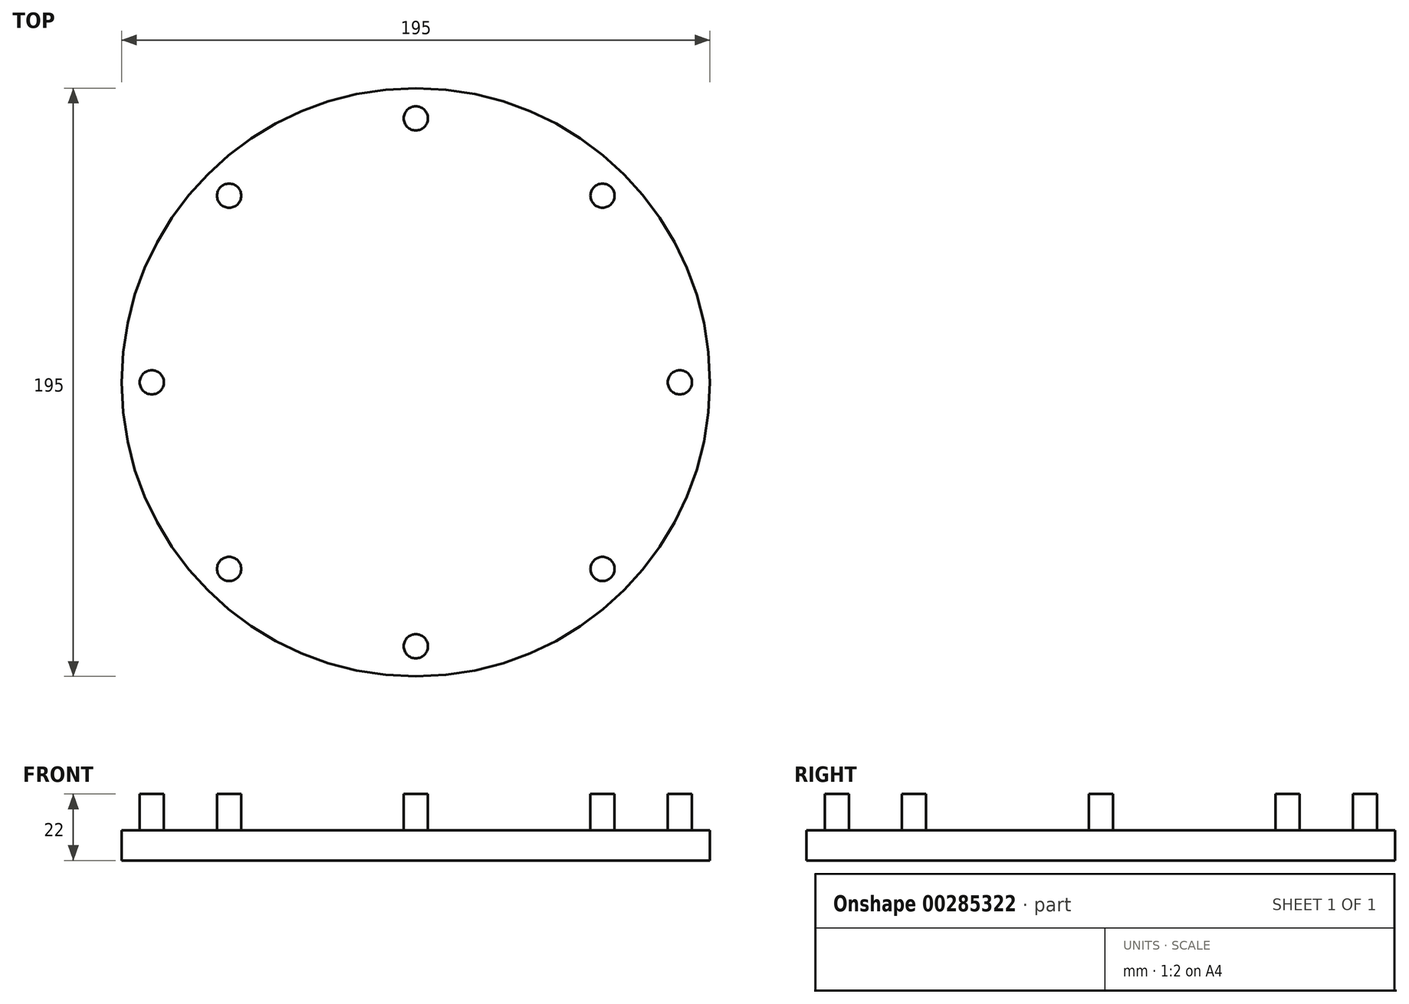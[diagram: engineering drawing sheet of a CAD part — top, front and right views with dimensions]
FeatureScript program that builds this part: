
annotation { "Feature Type Name" : "Feature", "Feature Type Description" : "" }
export const myFeature = defineFeature(function(context is Context, id is Id, definition is map)
    precondition{}
    {
        {
            var Q0;
            Q0=qCreatedBy(makeId("Top.planeOp"),FACE);
            var sketch = newSketch(context, id + "F0", { "sketchPlane" : qUnion([Q0])});
            skCircle(sketch, "E0", {"center": v(0, 0) * mm, "radius": 97.5 * mm});
            skCircle(sketch, "E1.cCircle", {"center": v(0, 0) * mm, "radius": 87.5 * mm, "construction": true});
            skLineSegment(sketch, "E1.0", {"start": v(87.5, 0) * mm, "end": v(61.87, -61.87) * mm});
            skLineSegment(sketch, "E1.1", {"start": v(61.87, -61.87) * mm, "end": v(0, -87.5) * mm});
            skLineSegment(sketch, "E1.2", {"start": v(0, -87.5) * mm, "end": v(-61.87, -61.87) * mm});
            skLineSegment(sketch, "E1.3", {"start": v(-61.87, -61.87) * mm, "end": v(-87.5, 0) * mm});
            skLineSegment(sketch, "E1.4", {"start": v(-87.5, 0) * mm, "end": v(-61.87, 61.87) * mm});
            skLineSegment(sketch, "E1.5", {"start": v(-61.87, 61.87) * mm, "end": v(0, 87.5) * mm});
            skLineSegment(sketch, "E1.6", {"start": v(0, 87.5) * mm, "end": v(61.87, 61.87) * mm});
            skLineSegment(sketch, "E1.7", {"start": v(61.87, 61.87) * mm, "end": v(87.5, 0) * mm});
            skCircle(sketch, "E2", {"center": v(0, 87.5) * mm, "radius": 4 * mm});
            skCircle(sketch, "E3", {"center": v(61.87, 61.87) * mm, "radius": 4 * mm});
            skCircle(sketch, "E4", {"center": v(87.5, 0) * mm, "radius": 4 * mm});
            skCircle(sketch, "E5", {"center": v(61.87, -61.87) * mm, "radius": 4 * mm});
            skCircle(sketch, "E6", {"center": v(0, -87.5) * mm, "radius": 4 * mm});
            skCircle(sketch, "E7", {"center": v(-61.87, -61.87) * mm, "radius": 4 * mm});
            skCircle(sketch, "E8", {"center": v(-87.5, 0) * mm, "radius": 4 * mm});
            skCircle(sketch, "E9", {"center": v(-61.87, 61.87) * mm, "radius": 4 * mm});
            skSolve(sketch);
        }
        {
            var Q0;
            {var subQ3=sQuery(id+"F0.wireOp",EDGE,"E4");var subQ15=sQuery(id+"F0.wireOp",EDGE,"E1.0");var subQ16=makeQuery(id+"F0.imprint","INTERSECT",VERTEX,{"derivedFrom":[subQ15,subQ3]});Q0=makeQuery(id+"F0.imprint","IMPRINT",FACE,{"disambiguationData":[TD([[makeQuery(id+"F0.imprint","IMPRINT",EDGE,{"disambiguationData":[TD([[subQ16,-1.0]])],"derivedFrom":subQ15}),-1.0]])]});}
            var Q1;
            {var subQ0=sQuery(id+"F0.wireOp",EDGE,"E1.5");var subQ1=sQuery(id+"F0.wireOp",EDGE,"E1.4");var subQ2=makeQuery(id+"F0.imprint","INTERSECT",VERTEX,{"derivedFrom":[subQ1,subQ0]});Q1=makeQuery(id+"F0.imprint","IMPRINT",FACE,{"disambiguationData":[TD([[makeQuery(id+"F0.imprint","IMPRINT",EDGE,{"disambiguationData":[TD([[subQ2,1.0]])],"derivedFrom":subQ1}),1.0]])]});}
            var Q2;
            {var subQ0=sQuery(id+"F0.wireOp",EDGE,"E1.5");var subQ1=sQuery(id+"F0.wireOp",EDGE,"E1.4");var subQ2=makeQuery(id+"F0.imprint","INTERSECT",VERTEX,{"derivedFrom":[subQ1,subQ0]});Q2=makeQuery(id+"F0.imprint","IMPRINT",FACE,{"disambiguationData":[TD([[makeQuery(id+"F0.imprint","IMPRINT",EDGE,{"disambiguationData":[TD([[subQ2,1.0]])],"derivedFrom":subQ1}),-1.0]])]});}
            var Q3;
            Q3=makeQuery(id+"F0.imprint","IMPRINT",FACE,{"disambiguationData":[TD([[makeQuery(id+"F0.imprint","IMPRINT",EDGE,{"derivedFrom":sQuery(id+"F0.wireOp",EDGE,"E0")}),1.0]])]});
            var Q4;
            {var subQ0=sQuery(id+"F0.wireOp",EDGE,"E1.6");var subQ1=sQuery(id+"F0.wireOp",EDGE,"E1.5");var subQ2=makeQuery(id+"F0.imprint","INTERSECT",VERTEX,{"derivedFrom":[subQ1,subQ0]});Q4=makeQuery(id+"F0.imprint","IMPRINT",FACE,{"disambiguationData":[TD([[makeQuery(id+"F0.imprint","IMPRINT",EDGE,{"disambiguationData":[TD([[subQ2,1.0]])],"derivedFrom":subQ1}),1.0]])]});}
            var Q5;
            {var subQ0=sQuery(id+"F0.wireOp",EDGE,"E1.6");var subQ1=sQuery(id+"F0.wireOp",EDGE,"E1.5");var subQ2=makeQuery(id+"F0.imprint","INTERSECT",VERTEX,{"derivedFrom":[subQ1,subQ0]});Q5=makeQuery(id+"F0.imprint","IMPRINT",FACE,{"disambiguationData":[TD([[makeQuery(id+"F0.imprint","IMPRINT",EDGE,{"disambiguationData":[TD([[subQ2,1.0]])],"derivedFrom":subQ1}),-1.0]])]});}
            var Q6;
            {var subQ0=sQuery(id+"F0.wireOp",EDGE,"E1.7");var subQ1=sQuery(id+"F0.wireOp",EDGE,"E1.6");var subQ2=makeQuery(id+"F0.imprint","INTERSECT",VERTEX,{"derivedFrom":[subQ1,subQ0]});Q6=makeQuery(id+"F0.imprint","IMPRINT",FACE,{"disambiguationData":[TD([[makeQuery(id+"F0.imprint","IMPRINT",EDGE,{"disambiguationData":[TD([[subQ2,1.0]])],"derivedFrom":subQ1}),-1.0]])]});}
            var Q7;
            {var subQ0=sQuery(id+"F0.wireOp",EDGE,"E1.7");var subQ1=sQuery(id+"F0.wireOp",EDGE,"E1.6");var subQ2=makeQuery(id+"F0.imprint","INTERSECT",VERTEX,{"derivedFrom":[subQ1,subQ0]});Q7=makeQuery(id+"F0.imprint","IMPRINT",FACE,{"disambiguationData":[TD([[makeQuery(id+"F0.imprint","IMPRINT",EDGE,{"disambiguationData":[TD([[subQ2,1.0]])],"derivedFrom":subQ1}),1.0]])]});}
            var Q8;
            {var subQ0=sQuery(id+"F0.wireOp",EDGE,"E1.7");var subQ1=sQuery(id+"F0.wireOp",EDGE,"E1.0");var subQ2=makeQuery(id+"F0.imprint","INTERSECT",VERTEX,{"derivedFrom":[subQ1,subQ0]});Q8=makeQuery(id+"F0.imprint","IMPRINT",FACE,{"disambiguationData":[TD([[makeQuery(id+"F0.imprint","IMPRINT",EDGE,{"disambiguationData":[TD([[subQ2,-1.0]])],"derivedFrom":subQ1}),-1.0]])]});}
            var Q9;
            {var subQ0=sQuery(id+"F0.wireOp",EDGE,"E1.7");var subQ1=sQuery(id+"F0.wireOp",EDGE,"E1.0");var subQ2=makeQuery(id+"F0.imprint","INTERSECT",VERTEX,{"derivedFrom":[subQ1,subQ0]});Q9=makeQuery(id+"F0.imprint","IMPRINT",FACE,{"disambiguationData":[TD([[makeQuery(id+"F0.imprint","IMPRINT",EDGE,{"disambiguationData":[TD([[subQ2,-1.0]])],"derivedFrom":subQ1}),1.0]])]});}
            var Q10;
            {var subQ0=sQuery(id+"F0.wireOp",EDGE,"E1.1");var subQ1=sQuery(id+"F0.wireOp",EDGE,"E1.0");var subQ2=makeQuery(id+"F0.imprint","INTERSECT",VERTEX,{"derivedFrom":[subQ1,subQ0]});Q10=makeQuery(id+"F0.imprint","IMPRINT",FACE,{"disambiguationData":[TD([[makeQuery(id+"F0.imprint","IMPRINT",EDGE,{"disambiguationData":[TD([[subQ2,1.0]])],"derivedFrom":subQ1}),-1.0]])]});}
            var Q11;
            {var subQ0=sQuery(id+"F0.wireOp",EDGE,"E1.1");var subQ1=sQuery(id+"F0.wireOp",EDGE,"E1.0");var subQ2=makeQuery(id+"F0.imprint","INTERSECT",VERTEX,{"derivedFrom":[subQ1,subQ0]});Q11=makeQuery(id+"F0.imprint","IMPRINT",FACE,{"disambiguationData":[TD([[makeQuery(id+"F0.imprint","IMPRINT",EDGE,{"disambiguationData":[TD([[subQ2,1.0]])],"derivedFrom":subQ1}),1.0]])]});}
            var Q12;
            {var subQ0=sQuery(id+"F0.wireOp",EDGE,"E1.2");var subQ1=sQuery(id+"F0.wireOp",EDGE,"E1.1");var subQ2=makeQuery(id+"F0.imprint","INTERSECT",VERTEX,{"derivedFrom":[subQ1,subQ0]});Q12=makeQuery(id+"F0.imprint","IMPRINT",FACE,{"disambiguationData":[TD([[makeQuery(id+"F0.imprint","IMPRINT",EDGE,{"disambiguationData":[TD([[subQ2,1.0]])],"derivedFrom":subQ1}),-1.0]])]});}
            var Q13;
            {var subQ0=sQuery(id+"F0.wireOp",EDGE,"E1.2");var subQ1=sQuery(id+"F0.wireOp",EDGE,"E1.1");var subQ2=makeQuery(id+"F0.imprint","INTERSECT",VERTEX,{"derivedFrom":[subQ1,subQ0]});Q13=makeQuery(id+"F0.imprint","IMPRINT",FACE,{"disambiguationData":[TD([[makeQuery(id+"F0.imprint","IMPRINT",EDGE,{"disambiguationData":[TD([[subQ2,1.0]])],"derivedFrom":subQ1}),1.0]])]});}
            var Q14;
            {var subQ0=sQuery(id+"F0.wireOp",EDGE,"E1.3");var subQ1=sQuery(id+"F0.wireOp",EDGE,"E1.2");var subQ2=makeQuery(id+"F0.imprint","INTERSECT",VERTEX,{"derivedFrom":[subQ1,subQ0]});Q14=makeQuery(id+"F0.imprint","IMPRINT",FACE,{"disambiguationData":[TD([[makeQuery(id+"F0.imprint","IMPRINT",EDGE,{"disambiguationData":[TD([[subQ2,1.0]])],"derivedFrom":subQ1}),-1.0]])]});}
            var Q15;
            {var subQ0=sQuery(id+"F0.wireOp",EDGE,"E1.3");var subQ1=sQuery(id+"F0.wireOp",EDGE,"E1.2");var subQ2=makeQuery(id+"F0.imprint","INTERSECT",VERTEX,{"derivedFrom":[subQ1,subQ0]});Q15=makeQuery(id+"F0.imprint","IMPRINT",FACE,{"disambiguationData":[TD([[makeQuery(id+"F0.imprint","IMPRINT",EDGE,{"disambiguationData":[TD([[subQ2,1.0]])],"derivedFrom":subQ1}),1.0]])]});}
            var Q16;
            {var subQ0=sQuery(id+"F0.wireOp",EDGE,"E1.4");var subQ1=sQuery(id+"F0.wireOp",EDGE,"E1.3");var subQ2=makeQuery(id+"F0.imprint","INTERSECT",VERTEX,{"derivedFrom":[subQ1,subQ0]});Q16=makeQuery(id+"F0.imprint","IMPRINT",FACE,{"disambiguationData":[TD([[makeQuery(id+"F0.imprint","IMPRINT",EDGE,{"disambiguationData":[TD([[subQ2,1.0]])],"derivedFrom":subQ1}),-1.0]])]});}
            var Q17;
            {var subQ0=sQuery(id+"F0.wireOp",EDGE,"E1.4");var subQ1=sQuery(id+"F0.wireOp",EDGE,"E1.3");var subQ2=makeQuery(id+"F0.imprint","INTERSECT",VERTEX,{"derivedFrom":[subQ1,subQ0]});Q17=makeQuery(id+"F0.imprint","IMPRINT",FACE,{"disambiguationData":[TD([[makeQuery(id+"F0.imprint","IMPRINT",EDGE,{"disambiguationData":[TD([[subQ2,1.0]])],"derivedFrom":subQ1}),1.0]])]});}
            extrude(context, id + "F1", {"entities" : qUnion([Q0, Q1, Q2, Q3, Q4, Q5, Q6, Q7, Q8, Q9, Q10, Q11, Q12, Q13, Q14, Q15, Q16, Q17]), "depth" : 10 * mm});
        }
        {
            var Q0;
            {var subQ0=sQuery(id+"F0.wireOp",EDGE,"E1.6");var subQ1=sQuery(id+"F0.wireOp",EDGE,"E1.5");var subQ2=makeQuery(id+"F0.imprint","INTERSECT",VERTEX,{"derivedFrom":[subQ1,subQ0]});Q0=makeQuery(id+"F0.imprint","IMPRINT",FACE,{"disambiguationData":[TD([[makeQuery(id+"F0.imprint","IMPRINT",EDGE,{"disambiguationData":[TD([[subQ2,1.0]])],"derivedFrom":subQ1}),1.0]])]});}
            var Q1;
            {var subQ0=sQuery(id+"F0.wireOp",EDGE,"E1.6");var subQ1=sQuery(id+"F0.wireOp",EDGE,"E1.5");var subQ2=makeQuery(id+"F0.imprint","INTERSECT",VERTEX,{"derivedFrom":[subQ1,subQ0]});Q1=makeQuery(id+"F0.imprint","IMPRINT",FACE,{"disambiguationData":[TD([[makeQuery(id+"F0.imprint","IMPRINT",EDGE,{"disambiguationData":[TD([[subQ2,1.0]])],"derivedFrom":subQ1}),-1.0]])]});}
            var Q2;
            {var subQ0=sQuery(id+"F0.wireOp",EDGE,"E1.5");var subQ1=sQuery(id+"F0.wireOp",EDGE,"E1.4");var subQ2=makeQuery(id+"F0.imprint","INTERSECT",VERTEX,{"derivedFrom":[subQ1,subQ0]});Q2=makeQuery(id+"F0.imprint","IMPRINT",FACE,{"disambiguationData":[TD([[makeQuery(id+"F0.imprint","IMPRINT",EDGE,{"disambiguationData":[TD([[subQ2,1.0]])],"derivedFrom":subQ1}),1.0]])]});}
            var Q3;
            {var subQ0=sQuery(id+"F0.wireOp",EDGE,"E1.5");var subQ1=sQuery(id+"F0.wireOp",EDGE,"E1.4");var subQ2=makeQuery(id+"F0.imprint","INTERSECT",VERTEX,{"derivedFrom":[subQ1,subQ0]});Q3=makeQuery(id+"F0.imprint","IMPRINT",FACE,{"disambiguationData":[TD([[makeQuery(id+"F0.imprint","IMPRINT",EDGE,{"disambiguationData":[TD([[subQ2,1.0]])],"derivedFrom":subQ1}),-1.0]])]});}
            var Q4;
            {var subQ0=sQuery(id+"F0.wireOp",EDGE,"E1.4");var subQ1=sQuery(id+"F0.wireOp",EDGE,"E1.3");var subQ2=makeQuery(id+"F0.imprint","INTERSECT",VERTEX,{"derivedFrom":[subQ1,subQ0]});Q4=makeQuery(id+"F0.imprint","IMPRINT",FACE,{"disambiguationData":[TD([[makeQuery(id+"F0.imprint","IMPRINT",EDGE,{"disambiguationData":[TD([[subQ2,1.0]])],"derivedFrom":subQ1}),1.0]])]});}
            var Q5;
            {var subQ0=sQuery(id+"F0.wireOp",EDGE,"E1.4");var subQ1=sQuery(id+"F0.wireOp",EDGE,"E1.3");var subQ2=makeQuery(id+"F0.imprint","INTERSECT",VERTEX,{"derivedFrom":[subQ1,subQ0]});Q5=makeQuery(id+"F0.imprint","IMPRINT",FACE,{"disambiguationData":[TD([[makeQuery(id+"F0.imprint","IMPRINT",EDGE,{"disambiguationData":[TD([[subQ2,1.0]])],"derivedFrom":subQ1}),-1.0]])]});}
            var Q6;
            {var subQ0=sQuery(id+"F0.wireOp",EDGE,"E1.3");var subQ1=sQuery(id+"F0.wireOp",EDGE,"E1.2");var subQ2=makeQuery(id+"F0.imprint","INTERSECT",VERTEX,{"derivedFrom":[subQ1,subQ0]});Q6=makeQuery(id+"F0.imprint","IMPRINT",FACE,{"disambiguationData":[TD([[makeQuery(id+"F0.imprint","IMPRINT",EDGE,{"disambiguationData":[TD([[subQ2,1.0]])],"derivedFrom":subQ1}),1.0]])]});}
            var Q7;
            {var subQ0=sQuery(id+"F0.wireOp",EDGE,"E1.3");var subQ1=sQuery(id+"F0.wireOp",EDGE,"E1.2");var subQ2=makeQuery(id+"F0.imprint","INTERSECT",VERTEX,{"derivedFrom":[subQ1,subQ0]});Q7=makeQuery(id+"F0.imprint","IMPRINT",FACE,{"disambiguationData":[TD([[makeQuery(id+"F0.imprint","IMPRINT",EDGE,{"disambiguationData":[TD([[subQ2,1.0]])],"derivedFrom":subQ1}),-1.0]])]});}
            var Q8;
            {var subQ0=sQuery(id+"F0.wireOp",EDGE,"E1.2");var subQ1=sQuery(id+"F0.wireOp",EDGE,"E1.1");var subQ2=makeQuery(id+"F0.imprint","INTERSECT",VERTEX,{"derivedFrom":[subQ1,subQ0]});Q8=makeQuery(id+"F0.imprint","IMPRINT",FACE,{"disambiguationData":[TD([[makeQuery(id+"F0.imprint","IMPRINT",EDGE,{"disambiguationData":[TD([[subQ2,1.0]])],"derivedFrom":subQ1}),1.0]])]});}
            var Q9;
            {var subQ0=sQuery(id+"F0.wireOp",EDGE,"E1.2");var subQ1=sQuery(id+"F0.wireOp",EDGE,"E1.1");var subQ2=makeQuery(id+"F0.imprint","INTERSECT",VERTEX,{"derivedFrom":[subQ1,subQ0]});Q9=makeQuery(id+"F0.imprint","IMPRINT",FACE,{"disambiguationData":[TD([[makeQuery(id+"F0.imprint","IMPRINT",EDGE,{"disambiguationData":[TD([[subQ2,1.0]])],"derivedFrom":subQ1}),-1.0]])]});}
            var Q10;
            {var subQ0=sQuery(id+"F0.wireOp",EDGE,"E1.1");var subQ1=sQuery(id+"F0.wireOp",EDGE,"E1.0");var subQ2=makeQuery(id+"F0.imprint","INTERSECT",VERTEX,{"derivedFrom":[subQ1,subQ0]});Q10=makeQuery(id+"F0.imprint","IMPRINT",FACE,{"disambiguationData":[TD([[makeQuery(id+"F0.imprint","IMPRINT",EDGE,{"disambiguationData":[TD([[subQ2,1.0]])],"derivedFrom":subQ1}),1.0]])]});}
            var Q11;
            {var subQ0=sQuery(id+"F0.wireOp",EDGE,"E1.1");var subQ1=sQuery(id+"F0.wireOp",EDGE,"E1.0");var subQ2=makeQuery(id+"F0.imprint","INTERSECT",VERTEX,{"derivedFrom":[subQ1,subQ0]});Q11=makeQuery(id+"F0.imprint","IMPRINT",FACE,{"disambiguationData":[TD([[makeQuery(id+"F0.imprint","IMPRINT",EDGE,{"disambiguationData":[TD([[subQ2,1.0]])],"derivedFrom":subQ1}),-1.0]])]});}
            var Q12;
            {var subQ0=sQuery(id+"F0.wireOp",EDGE,"E1.7");var subQ1=sQuery(id+"F0.wireOp",EDGE,"E1.0");var subQ2=makeQuery(id+"F0.imprint","INTERSECT",VERTEX,{"derivedFrom":[subQ1,subQ0]});Q12=makeQuery(id+"F0.imprint","IMPRINT",FACE,{"disambiguationData":[TD([[makeQuery(id+"F0.imprint","IMPRINT",EDGE,{"disambiguationData":[TD([[subQ2,-1.0]])],"derivedFrom":subQ1}),1.0]])]});}
            var Q13;
            {var subQ0=sQuery(id+"F0.wireOp",EDGE,"E1.7");var subQ1=sQuery(id+"F0.wireOp",EDGE,"E1.0");var subQ2=makeQuery(id+"F0.imprint","INTERSECT",VERTEX,{"derivedFrom":[subQ1,subQ0]});Q13=makeQuery(id+"F0.imprint","IMPRINT",FACE,{"disambiguationData":[TD([[makeQuery(id+"F0.imprint","IMPRINT",EDGE,{"disambiguationData":[TD([[subQ2,-1.0]])],"derivedFrom":subQ1}),-1.0]])]});}
            var Q14;
            {var subQ0=sQuery(id+"F0.wireOp",EDGE,"E1.7");var subQ1=sQuery(id+"F0.wireOp",EDGE,"E1.6");var subQ2=makeQuery(id+"F0.imprint","INTERSECT",VERTEX,{"derivedFrom":[subQ1,subQ0]});Q14=makeQuery(id+"F0.imprint","IMPRINT",FACE,{"disambiguationData":[TD([[makeQuery(id+"F0.imprint","IMPRINT",EDGE,{"disambiguationData":[TD([[subQ2,1.0]])],"derivedFrom":subQ1}),1.0]])]});}
            var Q15;
            {var subQ0=sQuery(id+"F0.wireOp",EDGE,"E1.7");var subQ1=sQuery(id+"F0.wireOp",EDGE,"E1.6");var subQ2=makeQuery(id+"F0.imprint","INTERSECT",VERTEX,{"derivedFrom":[subQ1,subQ0]});Q15=makeQuery(id+"F0.imprint","IMPRINT",FACE,{"disambiguationData":[TD([[makeQuery(id+"F0.imprint","IMPRINT",EDGE,{"disambiguationData":[TD([[subQ2,1.0]])],"derivedFrom":subQ1}),-1.0]])]});}
            extrude(context, id + "F2", {"entities" : qUnion([Q0, Q1, Q2, Q3, Q4, Q5, Q6, Q7, Q8, Q9, Q10, Q11, Q12, Q13, Q14, Q15]), "operationType" : NewBodyOperationType.ADD, "depth" : 22 * mm});
        }
    });
